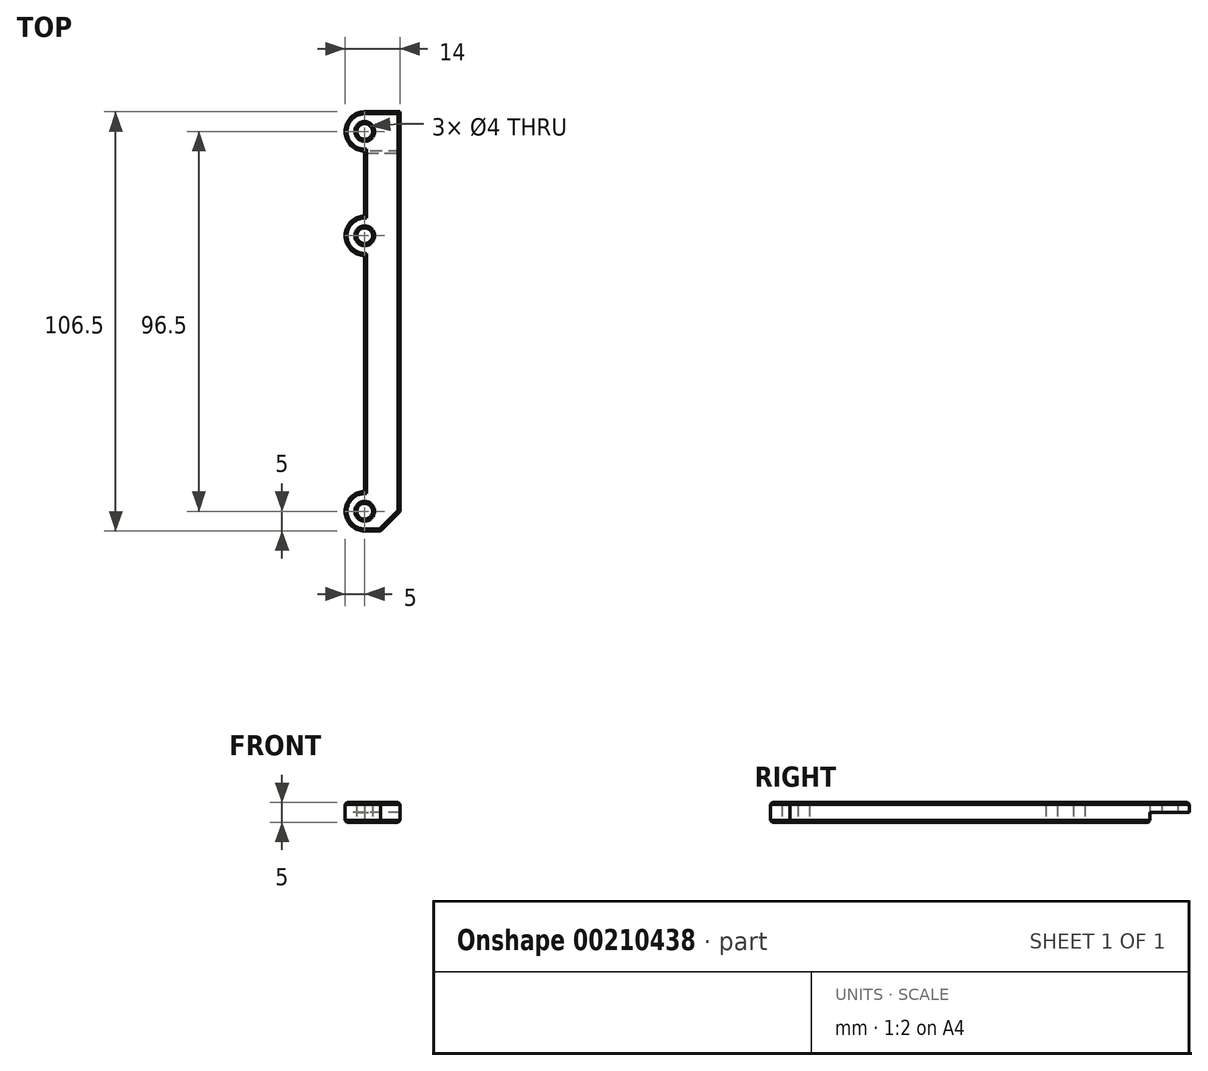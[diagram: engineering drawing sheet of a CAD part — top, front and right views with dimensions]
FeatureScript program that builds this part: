
annotation { "Feature Type Name" : "Feature", "Feature Type Description" : "" }
export const myFeature = defineFeature(function(context is Context, id is Id, definition is map)
    precondition{}
    {
        {
            var Q0;
            Q0=qCreatedBy(makeId("Top.planeOp"),FACE);
            var sketch = newSketch(context, id + "F0", { "sketchPlane" : qUnion([Q0])});
            skLineSegment(sketch, "E0.bottom", {"start": v(0, 0) * mm, "end": v(-9, 0) * mm});
            skLineSegment(sketch, "E0.top", {"start": v(0, 106.5) * mm, "end": v(-9, 106.5) * mm});
            skLineSegment(sketch, "E0.left", {"start": v(0, 0) * mm, "end": v(0, 106.5) * mm});
            skLineSegment(sketch, "E0.right", {"start": v(-9, 0) * mm, "end": v(-9, 106.5) * mm});
            skArc(sketch, "E1", {"start": v(-9, 106.5) * mm, "mid": v(-14, 101.5) * mm, "end": v(-9, 96.5) * mm});
            skArc(sketch, "E2", {"start": v(-9, 10) * mm, "mid": v(-14, 5) * mm, "end": v(-9, 0) * mm});
            skArc(sketch, "E3", {"start": v(-9, 80) * mm, "mid": v(-14, 75) * mm, "end": v(-9, 70) * mm});
            skLineSegment(sketch, "E4", {"start": v(-9, 80) * mm, "end": v(-9, 70) * mm});
            skCircle(sketch, "E5", {"center": v(-9, 101.5) * mm, "radius": 2 * mm});
            skCircle(sketch, "E6", {"center": v(-9, 75) * mm, "radius": 2 * mm});
            skCircle(sketch, "E7", {"center": v(-9, 5) * mm, "radius": 2 * mm});
            skSolve(sketch);
        }
        {
            var Q0;
            Q0=qSketchRegion(id+"F0",true);
            extrude(context, id + "F1", {"entities" : qUnion([Q0]), "depth" : 5 * mm});
        }
        {
            var Q0;
            Q0=makeQuery(id+"F1.opExtrude","CAP_FACE",FACE,{"disambiguationData":[OSD([sQuery(id+"F0.wireOp",EDGE,"E0.bottom"),sQuery(id+"F0.wireOp",EDGE,"E0.top"),sQuery(id+"F0.wireOp",EDGE,"E0.left"),sQuery(id+"F0.wireOp",EDGE,"E0.right"),sQuery(id+"F0.wireOp",EDGE,"E1"),sQuery(id+"F0.wireOp",EDGE,"E2"),sQuery(id+"F0.wireOp",EDGE,"E3"),sQuery(id+"F0.wireOp",EDGE,"E5"),sQuery(id+"F0.wireOp",EDGE,"E6"),sQuery(id+"F0.wireOp",EDGE,"E7")])],"isStart":true});
            var sketch = newSketch(context, id + "F2", { "sketchPlane" : qUnion([Q0])});
            skLineSegment(sketch, "E8", {"start": v(-9, -96.5) * mm, "end": v(0, -96.5) * mm});
            skLineSegment(sketch, "E9", {"start": v(0, -96.5) * mm, "end": v(0, -106.5) * mm});
            skLineSegment(sketch, "E10", {"start": v(0, -106.5) * mm, "end": v(-9, -106.5) * mm});
            skArc(sketch, "E11", {"start": v(-9, -96.5) * mm, "mid": v(-14, -101.5) * mm, "end": v(-9, -106.5) * mm});
            skSolve(sketch);
        }
        {
            var Q0;
            Q0 = qSketchRegion(id + "F2", true);
            extrude(context, id + "F3", {"entities" : qUnion([Q0]), "operationType" : NewBodyOperationType.REMOVE, "oppositeDirection" : true, "depth" : 2.5 * mm});
        }
        {
            var Q0;
            Q0=makeQuery(id+"F1.opExtrude","SWEPT_EDGE",EDGE,{"disambiguationData":[OSD([sQuery(id+"F0.wireOp",EDGE,"E0.bottom"),sQuery(id+"F0.wireOp",EDGE,"E0.left")])]});
            chamfer(context, id + "F4", {"entities" : qUnion([Q0]), "width" : 5 * mm, "tangentPropagation" : true});
        }
        {
            var Q0;
            Q0=makeQuery(id+"F1.opExtrude","CAP_FACE",FACE,{"disambiguationData":[OSD([sQuery(id+"F0.wireOp",EDGE,"E0.bottom"),sQuery(id+"F0.wireOp",EDGE,"E0.top"),sQuery(id+"F0.wireOp",EDGE,"E0.left"),sQuery(id+"F0.wireOp",EDGE,"E0.right"),sQuery(id+"F0.wireOp",EDGE,"E1"),sQuery(id+"F0.wireOp",EDGE,"E2"),sQuery(id+"F0.wireOp",EDGE,"E3"),sQuery(id+"F0.wireOp",EDGE,"E5"),sQuery(id+"F0.wireOp",EDGE,"E6"),sQuery(id+"F0.wireOp",EDGE,"E7")])],"isStart":false});
            var Q1;
            Q1=makeQuery(id+"F1.opExtrude","CAP_FACE",FACE,{"disambiguationData":[OSD([sQuery(id+"F0.wireOp",EDGE,"E0.bottom"),sQuery(id+"F0.wireOp",EDGE,"E0.top"),sQuery(id+"F0.wireOp",EDGE,"E0.left"),sQuery(id+"F0.wireOp",EDGE,"E0.right"),sQuery(id+"F0.wireOp",EDGE,"E1"),sQuery(id+"F0.wireOp",EDGE,"E2"),sQuery(id+"F0.wireOp",EDGE,"E3"),sQuery(id+"F0.wireOp",EDGE,"E5"),sQuery(id+"F0.wireOp",EDGE,"E6"),sQuery(id+"F0.wireOp",EDGE,"E7")])],"isStart":true});
            chamfer(context, id + "F5", {"entities" : qUnion([Q0, Q1]), "width" : .5 * mm, "tangentPropagation" : true});
        }
    });
